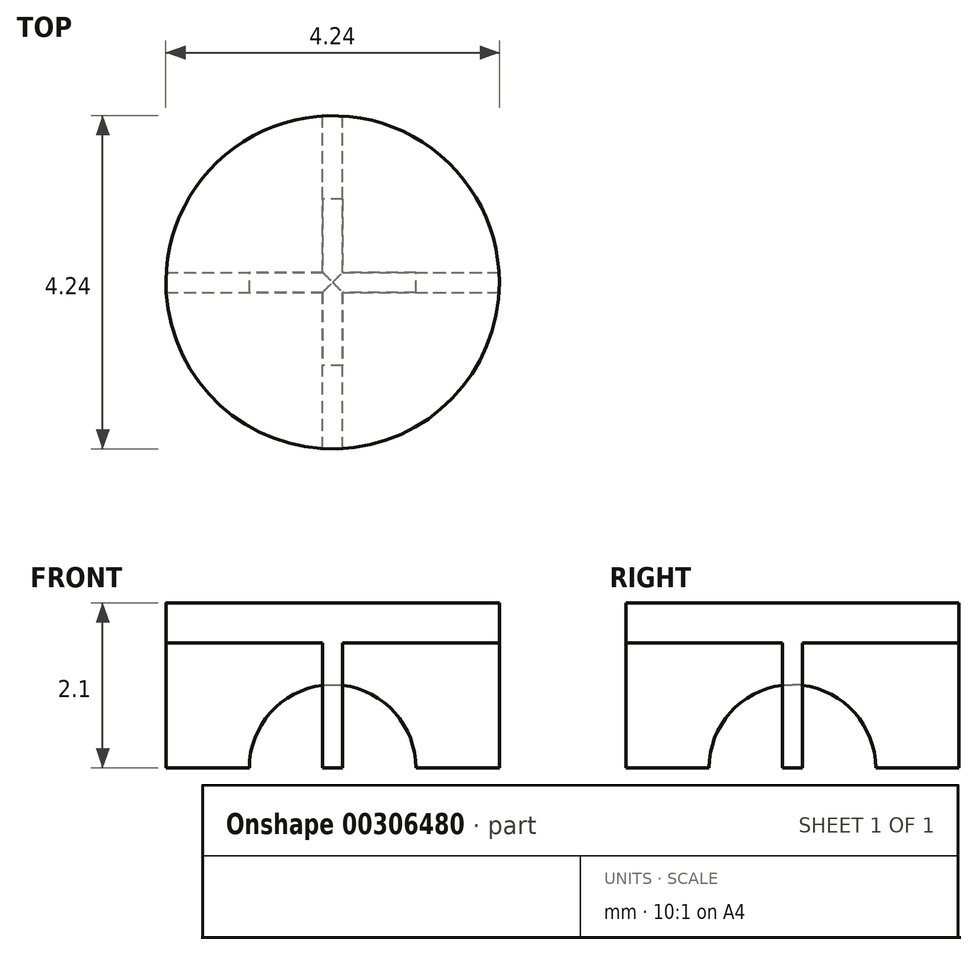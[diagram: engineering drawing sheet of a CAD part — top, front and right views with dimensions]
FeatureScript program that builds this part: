
annotation { "Feature Type Name" : "Feature", "Feature Type Description" : "" }
export const myFeature = defineFeature(function(context is Context, id is Id, definition is map)
    precondition{}
    {
        {
            var Q0;
            Q0=qCreatedBy(makeId("Front.planeOp"),FACE);
            var sketch = newSketch(context, id + "F0", { "sketchPlane" : qUnion([Q0])});
            skLineSegment(sketch, "E0.bottom", {"start": v(-2.12, 0) * mm, "end": v(2.12, 0) * mm});
            skLineSegment(sketch, "E0.top", {"start": v(-2.12, 1.59) * mm, "end": v(2.12, 1.59) * mm});
            skLineSegment(sketch, "E0.left", {"start": v(-2.12, 0) * mm, "end": v(-2.12, 1.59) * mm});
            skLineSegment(sketch, "E0.right", {"start": v(2.12, 0) * mm, "end": v(2.12, 1.59) * mm});
            skArc(sketch, "E1", {"start": v(-1.06, 0) * mm, "mid": v(0, 1.06) * mm, "end": v(1.06, 0) * mm});
            skSolve(sketch);
        }
        {
            var Q0;
            Q0=makeQuery(id+"F0.imprint","IMPRINT",FACE,{"disambiguationData":[TD([[makeQuery(id+"F0.imprint","IMPRINT",EDGE,{"derivedFrom":sQuery(id+"F0.wireOp",EDGE,"E0.top")}),-1.0]])]});
            extrude(context, id + "F1", {"entities" : qUnion([Q0]), "depth" : 0.13 * mm, "hasSecondDirection" : true, "secondDirectionOppositeDirection" : true, "secondDirectionDepth" : 0.13 * mm});
        }
        {
            var Q0;
            Q0=qCreatedBy(makeId("Right.planeOp"),FACE);
            var sketch = newSketch(context, id + "F2", { "sketchPlane" : qUnion([Q0])});
            skLineSegment(sketch, "E2.bottom", {"start": v(-2.12, 0) * mm, "end": v(2.12, 0) * mm});
            skLineSegment(sketch, "E2.top", {"start": v(-2.12, 1.59) * mm, "end": v(2.12, 1.59) * mm});
            skLineSegment(sketch, "E2.left", {"start": v(-2.12, 0) * mm, "end": v(-2.12, 1.59) * mm});
            skLineSegment(sketch, "E2.right", {"start": v(2.12, 0) * mm, "end": v(2.12, 1.59) * mm});
            skArc(sketch, "E3", {"start": v(-1.06, 0) * mm, "mid": v(0, 1.06) * mm, "end": v(1.06, 0) * mm});
            skSolve(sketch);
        }
        {
            var Q0;
            Q0=makeQuery(id+"F2.imprint","IMPRINT",FACE,{"disambiguationData":[TD([[makeQuery(id+"F2.imprint","IMPRINT",EDGE,{"derivedFrom":sQuery(id+"F2.wireOp",EDGE,"E2.top")}),-1.0]])]});
            extrude(context, id + "F3", {"entities" : qUnion([Q0]), "operationType" : NewBodyOperationType.ADD, "depth" : 0.13 * mm, "hasSecondDirection" : true, "secondDirectionOppositeDirection" : true, "secondDirectionDepth" : 0.13 * mm});
        }
        {
            var Q0;
            Q0=makeQuery(id+"F3.boolean.opBoolean","MERGE",FACE,{"derivedFrom":[makeQuery(id+"F1.opExtrude","SWEPT_FACE",FACE,{"disambiguationData":[OSD([sQuery(id+"F0.wireOp",EDGE,"E0.top")])]}),makeQuery(id+"F3.opExtrude","SWEPT_FACE",FACE,{"disambiguationData":[OSD([sQuery(id+"F2.wireOp",EDGE,"E2.top")])]})]});
            var sketch = newSketch(context, id + "F4", { "sketchPlane" : qUnion([Q0])});
            skCircle(sketch, "E4", {"center": v(0, 0) * mm, "radius": 2.12 * mm});
            skSolve(sketch);
        }
        {
            var Q0;
            Q0 = qSketchRegion(id + "F4", true);
            extrude(context, id + "F5", {"entities" : qUnion([Q0]), "operationType" : NewBodyOperationType.ADD, "depth" : 0.5 * mm, "offsetDistance" : 25.4 * mm});
        }
    });
